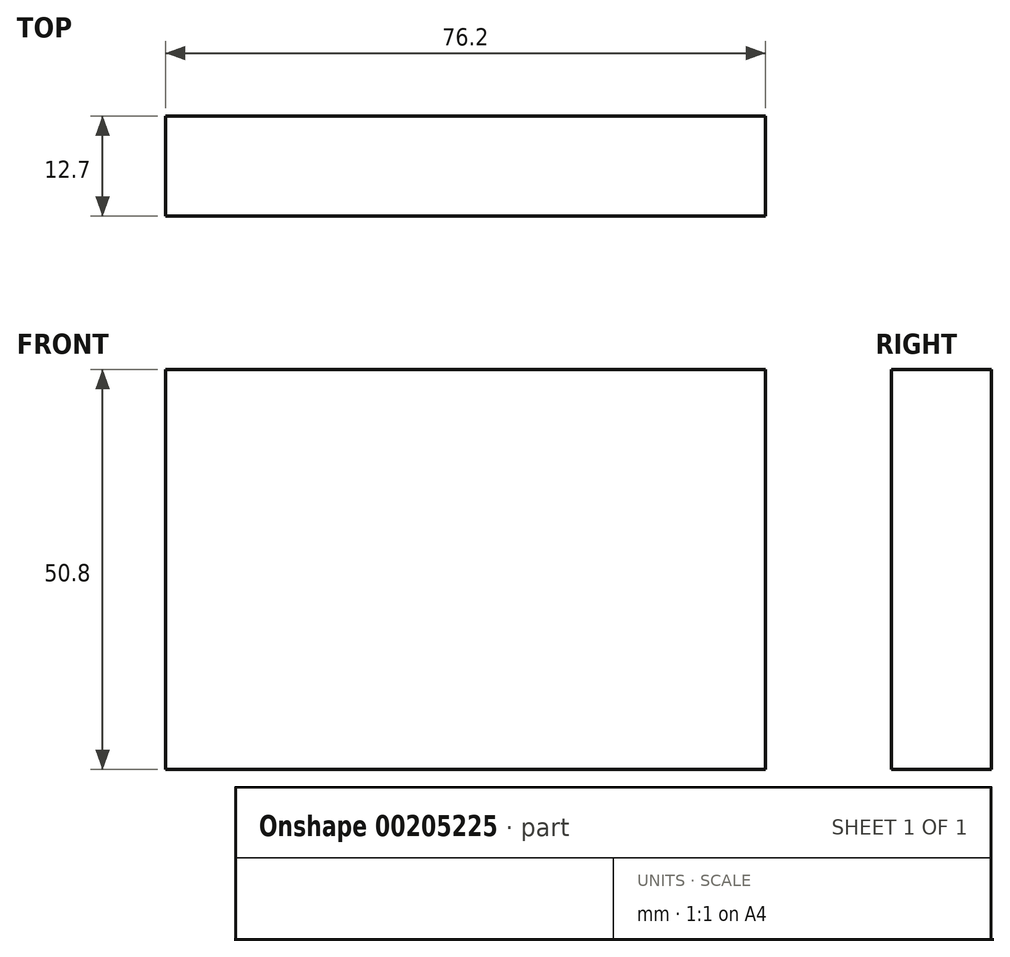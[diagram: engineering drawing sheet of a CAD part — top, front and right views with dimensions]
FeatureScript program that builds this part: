
annotation { "Feature Type Name" : "Feature", "Feature Type Description" : "" }
export const myFeature = defineFeature(function(context is Context, id is Id, definition is map)
    precondition{}
    {
        {
            var Q0;
            Q0=qCreatedBy(makeId("Front.planeOp"),FACE);
            var sketch = newSketch(context, id + "F0", { "sketchPlane" : qUnion([Q0])});
            skLineSegment(sketch, "E0.bottom", {"start": v(38.1, -25.4) * mm, "end": v(-38.1, -25.4) * mm});
            skLineSegment(sketch, "E0.top", {"start": v(38.1, 25.4) * mm, "end": v(-38.1, 25.4) * mm});
            skLineSegment(sketch, "E0.left", {"start": v(38.1, -25.4) * mm, "end": v(38.1, 25.4) * mm});
            skLineSegment(sketch, "E0.right", {"start": v(-38.1, -25.4) * mm, "end": v(-38.1, 25.4) * mm});
            skPoint(sketch, "E0.middle", {"position": v(0, 0) * mm});
            skSolve(sketch);
        }
        {
            var Q0;
            Q0 = qSketchRegion(id + "F0", true);
            extrude(context, id + "F1", {"entities" : qUnion([Q0]), "depth" : 12.7 * mm});
        }
    });
